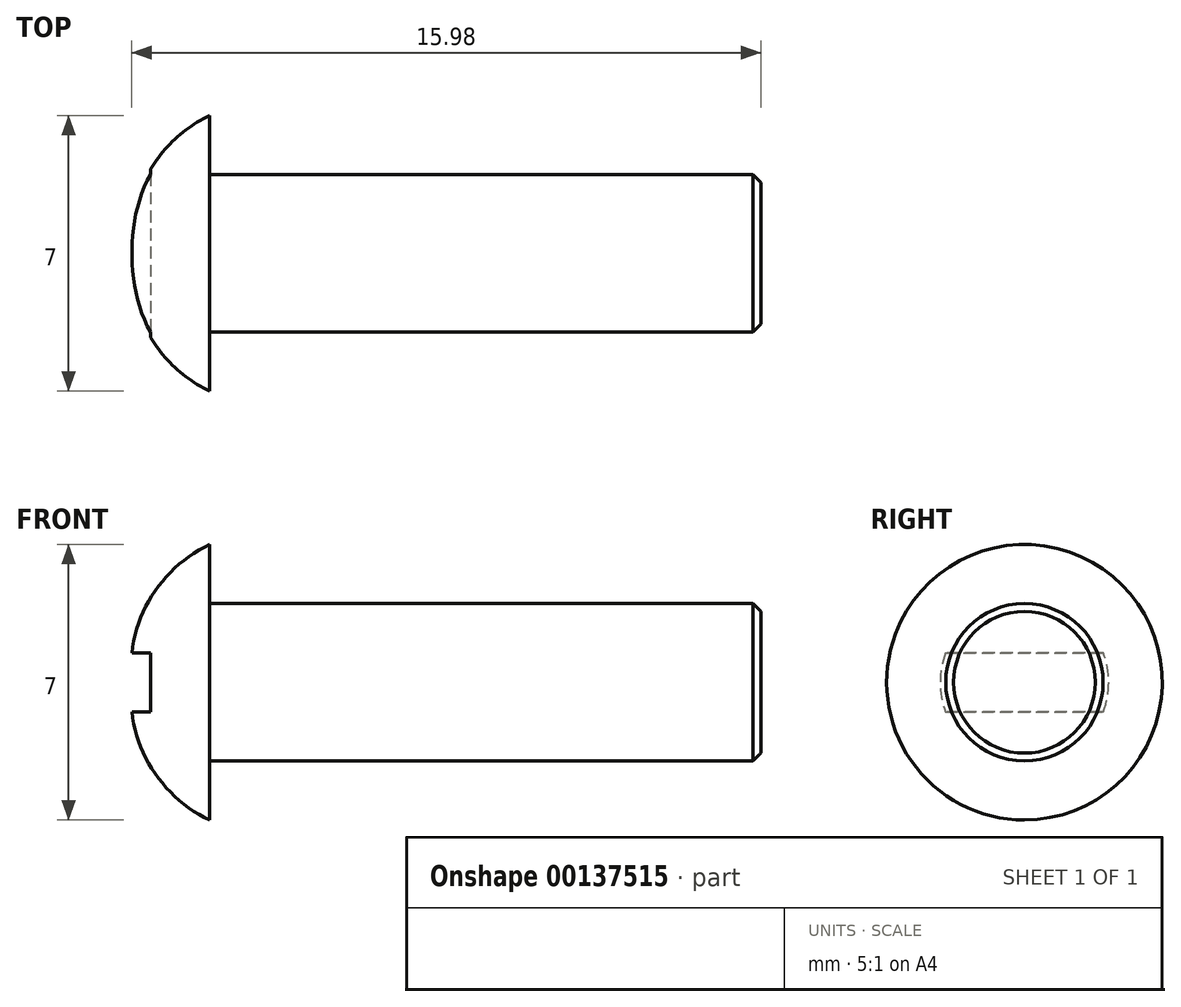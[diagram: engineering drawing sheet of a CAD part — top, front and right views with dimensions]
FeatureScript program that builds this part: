
annotation { "Feature Type Name" : "Feature", "Feature Type Description" : "" }
export const myFeature = defineFeature(function(context is Context, id is Id, definition is map)
    precondition{}
    {
        {
            var Q0;
            Q0=qCreatedBy(makeId("Front.planeOp"),FACE);
            var sketch = newSketch(context, id + "F0", { "sketchPlane" : qUnion([Q0])});
            skLineSegment(sketch, "E0.bottom", {"start": v(7.5, -2) * mm, "end": v(-6.5, -2) * mm});
            skLineSegment(sketch, "E0.top", {"start": v(7.5, 2) * mm, "end": v(-6.5, 2) * mm});
            skLineSegment(sketch, "E0.left", {"start": v(7.5, -2) * mm, "end": v(7.5, 2) * mm});
            skPoint(sketch, "E0.middle", {"position": v(0, 0) * mm});
            skLineSegment(sketch, "E1.bottom", {"start": v(-6.5, -3.5) * mm, "end": v(-8.5, -3.5) * mm});
            skLineSegment(sketch, "E1.top", {"start": v(-6.5, 3.5) * mm, "end": v(-8.5, 3.5) * mm});
            skLineSegment(sketch, "E1.left", {"start": v(-6.5, -3.5) * mm, "end": v(-6.5, 3.5) * mm});
            skLineSegment(sketch, "E1.right", {"start": v(-8.5, -3.5) * mm, "end": v(-8.5, 3.5) * mm});
            skPoint(sketch, "E1.middle", {"position": v(-7.5, 0) * mm});
            skLineSegment(sketch, "E2", {"start": v(7.5, 0) * mm, "end": v(-8.5, 0) * mm});
            skPoint(sketch, "E3.orphan", {"position": v(-7.5, -2) * mm});
            skPoint(sketch, "E4.orphan", {"position": v(-7.5, 2) * mm});
            skSolve(sketch);
        }
        {
            var Q0;
            {var subQ0=sQuery(id+"F0.wireOp",EDGE,"E0.left");var subQ1=sQuery(id+"F0.wireOp",EDGE,"E0.top");var subQ2=makeQuery(id+"F0.imprint","INTERSECT",VERTEX,{"derivedFrom":[subQ1,subQ0]});Q0=makeQuery(id+"F0.imprint","IMPRINT",FACE,{"disambiguationData":[TD([[makeQuery(id+"F0.imprint","IMPRINT",EDGE,{"disambiguationData":[TD([[subQ2,-1.0]])],"derivedFrom":subQ1}),1.0]])]});}
            var Q1;
            {var subQ1=sQuery(id+"F0.wireOp",EDGE,"E1.top");Q1=makeQuery(id+"F0.imprint","IMPRINT",FACE,{"disambiguationData":[TD([[makeQuery(id+"F0.imprint","IMPRINT",EDGE,{"derivedFrom":subQ1}),1.0]])]});}
            var Q2;
            Q2=sQuery(id+"F0.wireOp",EDGE,"E2");
            revolve(context, id + "F1", {"entities" : qUnion([Q0, Q1]), "axis" : qUnion([Q2]), "revolveType" : RevolveType.FULL});
        }
        {
            var Q0;
            Q0=makeQuery(id+"F1.opRevolve","SWEPT_EDGE",EDGE,{"disambiguationData":[OSD([sQuery(id+"F0.wireOp",EDGE,"E1.top"),sQuery(id+"F0.wireOp",EDGE,"E1.right")])]});
            fillet(context, id + "F2", {"entities" : qUnion([Q0]), "radius" : 3.5 * mm, "tangentPropagation" : true, "allowEdgeOverflow" : false});
        }
        {
            var Q0;
            Q0=makeQuery(id+"F1.opRevolve","SWEPT_EDGE",EDGE,{"disambiguationData":[OSD([sQuery(id+"F0.wireOp",EDGE,"E0.top"),sQuery(id+"F0.wireOp",EDGE,"E0.left")])]});
            chamfer(context, id + "F3", {"entities" : qUnion([Q0]), "width" : 0.2 * mm, "tangentPropagation" : true});
        }
        {
            var Q0;
            {var subQ1=sQuery(id+"F0.wireOp",EDGE,"E1.bottom");Q0=makeQuery(id+"F0.imprint","IMPRINT",FACE,{"disambiguationData":[TD([[makeQuery(id+"F0.imprint","IMPRINT",EDGE,{"derivedFrom":subQ1}),-1.0]])]});}
            var sketch = newSketch(context, id + "F4", { "sketchPlane" : qUnion([Q0])});
            skLineSegment(sketch, "E5.bottom", {"start": v(-8, 0.75) * mm, "end": v(-9.13, 0.75) * mm});
            skLineSegment(sketch, "E5.top", {"start": v(-8, -0.75) * mm, "end": v(-9.13, -0.75) * mm});
            skLineSegment(sketch, "E5.right", {"start": v(-9.13, 0.75) * mm, "end": v(-9.13, -0.75) * mm});
            skPoint(sketch, "E5.middle", {"position": v(-8.56, 0) * mm});
            skLineSegment(sketch, "E6", {"start": v(-8, -0.75) * mm, "end": v(-8, 0.75) * mm});
            skSolve(sketch);
        }
        {
            var Q0;
            Q0 = qSketchRegion(id + "F4", true);
            extrude(context, id + "F5", {"entities" : qUnion([Q0]), "operationType" : NewBodyOperationType.REMOVE, "oppositeDirection" : true, "depth" : 30 * mm, "symmetric" : true});
        }
    });
